# Revit family: Doppelnippel
name_source: partatom
category: HLS-Bauteile
revit_build: Autodesk Revit 2017 (Build: 20190507_1515(x64)
units: mm (PartAtom-declared; Revit-internal decimal feet)

## family parameters
Arbeitsebenenbasiert = Ja
Beim Laden mit Abzugskörper schneiden = Nein
Bemaßung runder Anschluss = Durchmesser verwenden
Gemeinsam genutzt = Ja
Immer vertikal = Nein
Raumberechnungspunkt = Nein
Teiletyp = Normal

## types (6) — shared parameters
D = 21 mm  [stored 0.0688976 ft]
D0 = 19 mm
Fabrikat = MEFA
Firma = MEFA Befestigungs- und Montagesysteme GmbH
Gewinde = 1/2''
Kurztext1 = Doppelnippel 1/2"
Material = Stahl
Mengeneinheit = St
Vorgabe-Ansicht = 1219 mm
vpe = 1 St

## per-type parameters (varying)
| type | Artikelnummer | EAN | Gewicht | Gewicht pro Bauteil | Kurztext2 | Länge |
| Doppelnippel 1/2" L=  40 | 0700403 | 4250928416117 | 0.05 kg | 0.05 kg | Länge 40 mm gvz | 40 mm  [stored 0.131234 ft] |
| Doppelnippel 1/2" L=  60 | 0700603 | 4250928416124 | 0.07 kg | 0.07 kg | Länge 60 mm gvz | 60 mm  [stored 0.19685 ft] |
| Doppelnippel 1/2" L=  80 | 0700803 | 4250928416131 | 0.10 kg | 0.10 kg | Länge 80 mm gvz | 80 mm  [stored 0.262467 ft] |
| Doppelnippel 1/2" L= 100 | 0701003 | 4250928416148 | 0.12 kg | 0.12 kg | Länge 100 mm gvz | 100 mm  [stored 0.328084 ft] |
| Doppelnippel 1/2" L= 120 | 0701203 | 4250928416155 | 0.15 kg | 0.15 kg | Länge 120 mm gvz | 120 mm  [stored 0.393701 ft] |
| Doppelnippel 1/2" L= 150 | 0701503 | 4250928416162 | 0.19 kg | 0.19 kg | Länge 150 mm gvz | 150 mm |

note: [stored X ft] marks values corroborated as IEEE doubles in the binary element streams (Revit-internal decimal feet)
